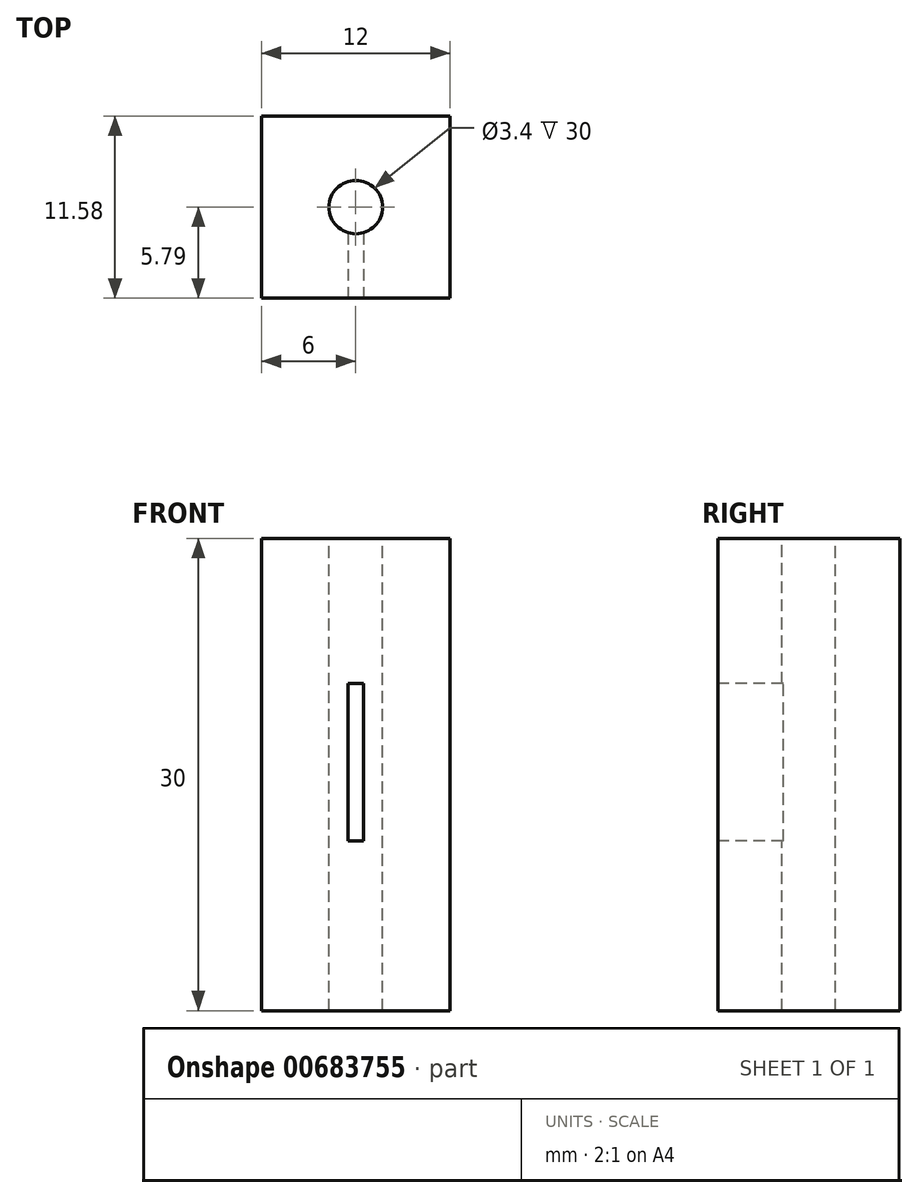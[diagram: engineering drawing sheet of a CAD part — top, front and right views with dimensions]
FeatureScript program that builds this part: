
annotation { "Feature Type Name" : "Feature", "Feature Type Description" : "" }
export const myFeature = defineFeature(function(context is Context, id is Id, definition is map)
    precondition{}
    {
        {
            var Q0;
            Q0=qCreatedBy(makeId("Top.planeOp"),FACE);
            var sketch = newSketch(context, id + "F0", { "sketchPlane" : qUnion([Q0])});
            skLineSegment(sketch, "E0.bottom", {"start": v(-6, 5.79) * mm, "end": v(6, 5.79) * mm});
            skLineSegment(sketch, "E0.top", {"start": v(-6, -5.79) * mm, "end": v(6, -5.79) * mm});
            skLineSegment(sketch, "E0.left", {"start": v(-6, 5.79) * mm, "end": v(-6, -5.79) * mm});
            skLineSegment(sketch, "E0.right", {"start": v(6, 5.79) * mm, "end": v(6, -5.79) * mm});
            skPoint(sketch, "E0.middle", {"position": v(0, 0) * mm});
            skSolve(sketch);
        }
        {
            var Q0;
            Q0 = qSketchRegion(id + "F0", true);
            extrude(context, id + "F1", {"entities" : qUnion([Q0]), "depth" : 30 * mm, "offsetDistance" : 25 * mm});
        }
        {
            var Q0;
            Q0=makeQuery(id+"F1.opExtrude","CAP_FACE",FACE,{"disambiguationData":[OSD([sQuery(id+"F0.wireOp",EDGE,"E0.bottom"),sQuery(id+"F0.wireOp",EDGE,"E0.top"),sQuery(id+"F0.wireOp",EDGE,"E0.left"),sQuery(id+"F0.wireOp",EDGE,"E0.right")])],"isStart":false});
            var sketch = newSketch(context, id + "F2", { "sketchPlane" : qUnion([Q0])});
            skCircle(sketch, "E1", {"center": v(0, 0) * mm, "radius": 1.7 * mm});
            skSolve(sketch);
        }
        {
            var Q0;
            Q0 = qSketchRegion(id + "F2", true);
            extrude(context, id + "F3", {"entities" : qUnion([Q0]), "operationType" : NewBodyOperationType.REMOVE, "oppositeDirection" : true, "depth" : 30 * mm, "offsetDistance" : 25 * mm});
        }
        {
            var Q0;
            Q0=makeQuery(id+"F1.opExtrude","SWEPT_FACE",FACE,{"disambiguationData":[OSD([sQuery(id+"F0.wireOp",EDGE,"E0.top")])]});
            var sketch = newSketch(context, id + "F4", { "sketchPlane" : qUnion([Q0])});
            skLineSegment(sketch, "E2.bottom", {"start": v(-0.5, 20.77) * mm, "end": v(0.5, 20.77) * mm});
            skLineSegment(sketch, "E2.top", {"start": v(-0.5, 10.77) * mm, "end": v(0.5, 10.77) * mm});
            skLineSegment(sketch, "E2.left", {"start": v(-0.5, 20.77) * mm, "end": v(-0.5, 10.77) * mm});
            skLineSegment(sketch, "E2.right", {"start": v(0.5, 20.77) * mm, "end": v(0.5, 10.77) * mm});
            skPoint(sketch, "E2.middle", {"position": v(0, 15.77) * mm});
            skSolve(sketch);
        }
        {
            var Q0;
            Q0 = qSketchRegion(id + "F4", true);
            extrude(context, id + "F5", {"entities" : qUnion([Q0]), "operationType" : NewBodyOperationType.REMOVE, "oppositeDirection" : true, "depth" : 6 * mm, "offsetDistance" : 25 * mm});
        }
    });
